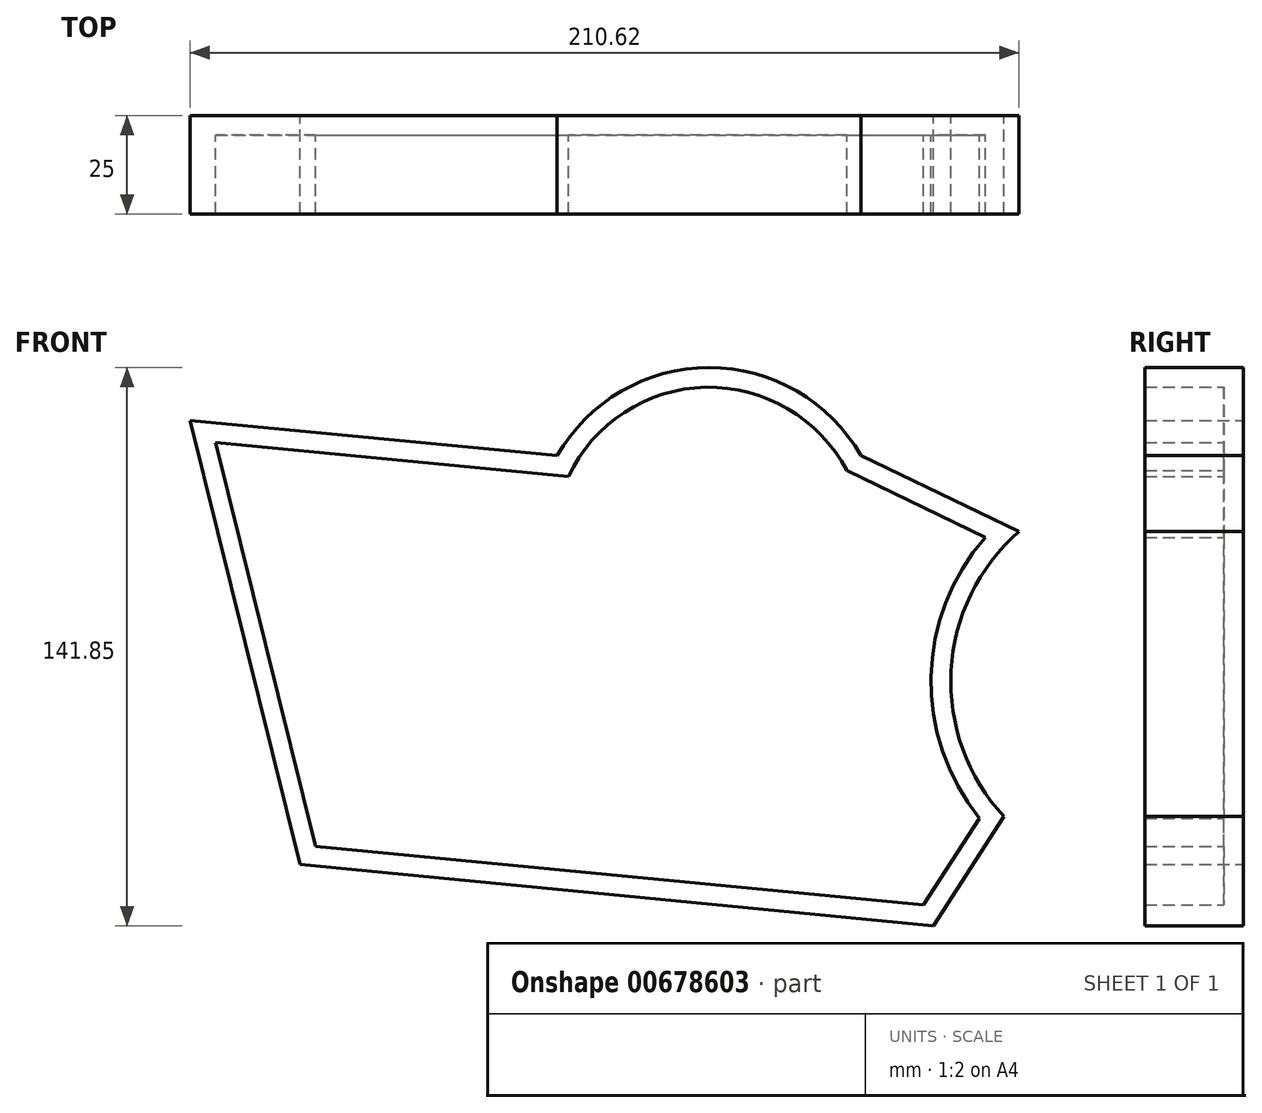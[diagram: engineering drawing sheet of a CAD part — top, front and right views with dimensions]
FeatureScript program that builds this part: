
annotation { "Feature Type Name" : "Feature", "Feature Type Description" : "" }
export const myFeature = defineFeature(function(context is Context, id is Id, definition is map)
    precondition{}
    {
        {
            var Q0;
            Q0=qCreatedBy(makeId("Front.planeOp"),FACE);
            var sketch = newSketch(context, id + "F0", { "sketchPlane" : qUnion([Q0])});
            skLineSegment(sketch, "E0", {"start": v(-69.37, -58.53) * mm, "end": v(91.57, -74.13) * mm});
            skLineSegment(sketch, "E1", {"start": v(91.57, -74.13) * mm, "end": v(109.54, -46.38) * mm});
            skLineSegment(sketch, "E2", {"start": v(-69.37, -58.53) * mm, "end": v(-97.29, 54.3) * mm});
            skLineSegment(sketch, "E3", {"start": v(-97.29, 54.3) * mm, "end": v(-4, 45.32) * mm});
            skArc(sketch, "E4", {"start": v(73.16, 45.32) * mm, "mid": v(34.58, 67.72) * mm, "end": v(-4, 45.32) * mm});
            skLineSegment(sketch, "E5", {"start": v(73.16, 45.32) * mm, "end": v(113.33, 26.03) * mm});
            skArc(sketch, "E6", {"start": v(113.33, 26.03) * mm, "mid": v(96.05, -9.37) * mm, "end": v(109.54, -46.38) * mm});
            skSolve(sketch);
        }
        {
            var Q0;
            Q0=makeQuery(id+"F0.imprint","IMPRINT",FACE,{"disambiguationData":[TD([[makeQuery(id+"F0.imprint","IMPRINT",EDGE,{"derivedFrom":sQuery(id+"F0.wireOp",EDGE,"E0")}),1.0]])]});
            extrude(context, id + "F1", {"entities" : qUnion([Q0]), "depth" : 25 * mm, "offsetDistance" : 25 * mm});
        }
        {
            var Q0;
            Q0=makeQuery(id+"F1.opExtrude","CAP_FACE",FACE,{"disambiguationData":[OSD([sQuery(id+"F0.wireOp",EDGE,"E0"),sQuery(id+"F0.wireOp",EDGE,"E1"),sQuery(id+"F0.wireOp",EDGE,"E2"),sQuery(id+"F0.wireOp",EDGE,"E3"),sQuery(id+"F0.wireOp",EDGE,"E4"),sQuery(id+"F0.wireOp",EDGE,"E5"),sQuery(id+"F0.wireOp",EDGE,"E6")])],"isStart":false});
            shell(context, id + "F2", {"entities" : qUnion([Q0]), "thickness" : 5 * mm});
        }
    });
